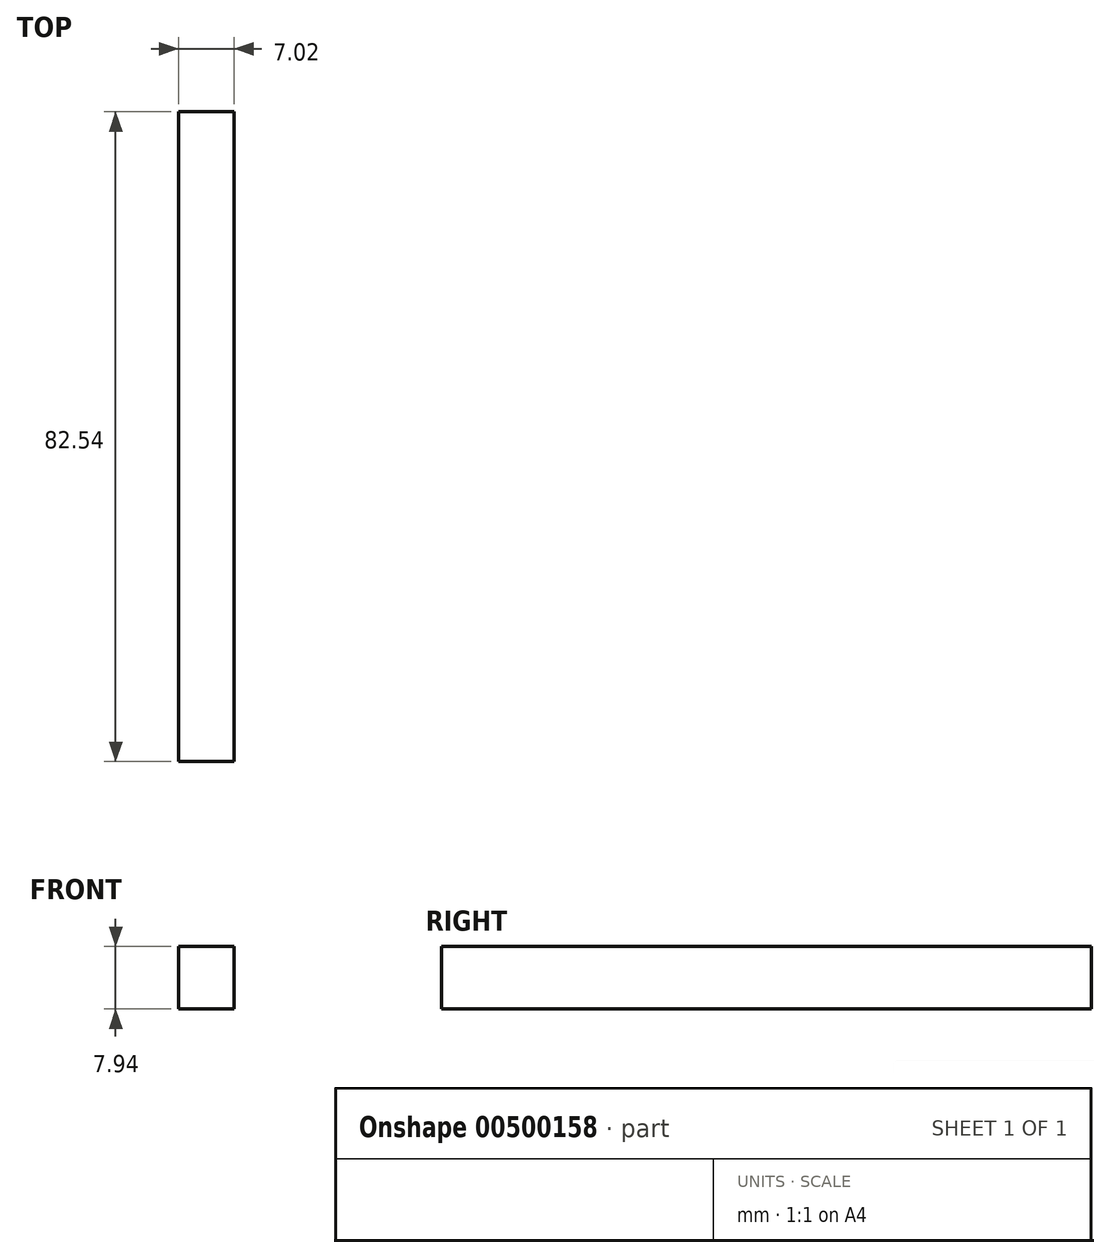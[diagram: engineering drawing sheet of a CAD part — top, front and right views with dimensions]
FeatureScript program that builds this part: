
annotation { "Feature Type Name" : "Feature", "Feature Type Description" : "" }
export const myFeature = defineFeature(function(context is Context, id is Id, definition is map)
    precondition{}
    {
        {
            var Q0;
            Q0=qCreatedBy(makeId("Front.planeOp"),FACE);
            var sketch = newSketch(context, id + "F0", { "sketchPlane" : qUnion([Q0])});
            skLineSegment(sketch, "E0.bottom", {"start": v(-3.5, 3.97) * mm, "end": v(3.5, 3.97) * mm});
            skLineSegment(sketch, "E0.top", {"start": v(-3.5, -3.97) * mm, "end": v(3.5, -3.97) * mm});
            skLineSegment(sketch, "E0.left", {"start": v(-3.5, 3.97) * mm, "end": v(-3.5, -3.97) * mm});
            skLineSegment(sketch, "E0.right", {"start": v(3.5, 3.97) * mm, "end": v(3.5, -3.97) * mm});
            skPoint(sketch, "E0.middle", {"position": v(0, 0) * mm});
            skSolve(sketch);
        }
        {
            var Q0;
            Q0=makeQuery(id+"F0.imprint","IMPRINT",FACE,{"disambiguationData":[TD([[makeQuery(id+"F0.imprint","IMPRINT",EDGE,{"derivedFrom":sQuery(id+"F0.wireOp",EDGE,"E0.bottom")}),-1.0]])]});
            extrude(context, id + "F1", {"entities" : qUnion([Q0]), "endBound" : BoundingType.SYMMETRIC, "depth" : 82.55 * mm});
        }
    });
